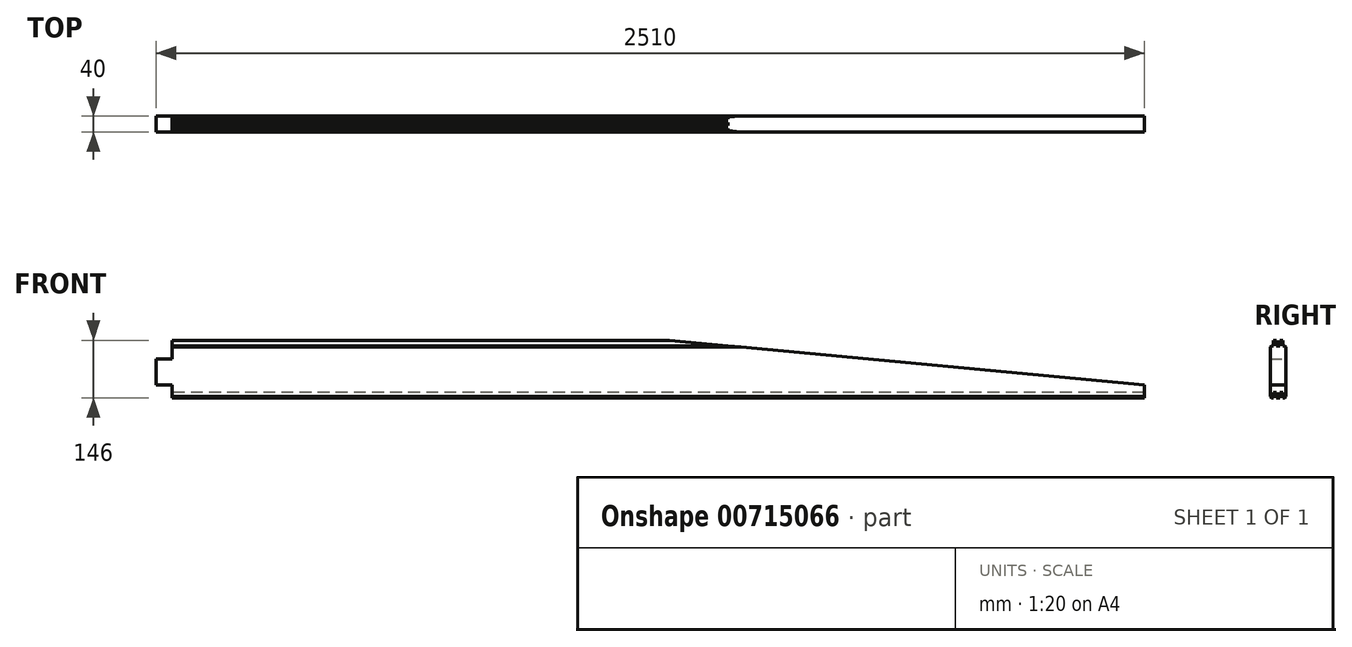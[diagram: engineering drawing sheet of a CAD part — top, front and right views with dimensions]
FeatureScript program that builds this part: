
annotation { "Feature Type Name" : "Feature", "Feature Type Description" : "" }
export const myFeature = defineFeature(function(context is Context, id is Id, definition is map)
    precondition{}
    {
        {
            assignVariable(context, id + "F0", {"name" : "Laenge", "anyValue" : 2550});
        }
        {
            var Q0;
            Q0=qCreatedBy(makeId("Right.planeOp"),FACE);
            var sketch = newSketch(context, id + "F1", { "sketchPlane" : qUnion([Q0])});
            skLineSegment(sketch, "E0", {"start": v(20, 63) * mm, "end": v(20, -63) * mm});
            skLineSegment(sketch, "E1", {"start": v(20, -63) * mm, "end": v(17, -66) * mm});
            skLineSegment(sketch, "E2", {"start": v(17, -66) * mm, "end": v(12, -66) * mm});
            skLineSegment(sketch, "E3", {"start": v(12, -52) * mm, "end": v(12, -66) * mm});
            skLineSegment(sketch, "E4", {"start": v(12, -52) * mm, "end": v(4, -52) * mm});
            skLineSegment(sketch, "E5", {"start": v(4, -66) * mm, "end": v(4, -52) * mm});
            skLineSegment(sketch, "E6", {"start": v(4, -66) * mm, "end": v(-4, -66) * mm});
            skLineSegment(sketch, "E7", {"start": v(-4, -52) * mm, "end": v(-4, -66) * mm});
            skLineSegment(sketch, "E8", {"start": v(-4, -52) * mm, "end": v(-12, -52) * mm});
            skLineSegment(sketch, "E9", {"start": v(-12, -66) * mm, "end": v(-12, -52) * mm});
            skLineSegment(sketch, "E10", {"start": v(-12, -66) * mm, "end": v(-17, -66) * mm});
            skLineSegment(sketch, "E11", {"start": v(-17, -66) * mm, "end": v(-20, -63) * mm});
            skLineSegment(sketch, "E12", {"start": v(-20, -63) * mm, "end": v(-20, 63) * mm});
            skLineSegment(sketch, "E13", {"start": v(-20, 63) * mm, "end": v(-17, 66) * mm});
            skLineSegment(sketch, "E14", {"start": v(-17, 66) * mm, "end": v(-12, 66) * mm});
            skLineSegment(sketch, "E15", {"start": v(-4, 66) * mm, "end": v(4, 66) * mm});
            skLineSegment(sketch, "E16", {"start": v(12, 66) * mm, "end": v(17, 66) * mm});
            skLineSegment(sketch, "E17", {"start": v(17, 66) * mm, "end": v(20, 63) * mm});
            skPoint(sketch, "E18.end.orphan", {"position": v(12, 57.8) * mm});
            skPoint(sketch, "E19.end.orphan", {"position": v(4, 66.3) * mm});
            skPoint(sketch, "E20.end.orphan", {"position": v(-4, 66.3) * mm});
            skLineSegment(sketch, "E21", {"start": v(-12, 66) * mm, "end": v(-12, 80) * mm});
            skLineSegment(sketch, "E22", {"start": v(-12, 80) * mm, "end": v(-4, 80) * mm});
            skLineSegment(sketch, "E23", {"start": v(-4, 80) * mm, "end": v(-4, 66) * mm});
            skLineSegment(sketch, "E24", {"start": v(4, 66) * mm, "end": v(4, 80) * mm});
            skLineSegment(sketch, "E25", {"start": v(4, 80) * mm, "end": v(12, 80) * mm});
            skLineSegment(sketch, "E26", {"start": v(12, 80) * mm, "end": v(12, 66) * mm});
            skLineSegment(sketch, "E27", {"start": v(20, -33) * mm, "end": v(-20, -33) * mm});
            skLineSegment(sketch, "E28", {"start": v(20, 33) * mm, "end": v(-20, 33) * mm});
            skPoint(sketch, "E29.end.orphan", {"position": v(-141.42, 0) * mm});
            skLineSegment(sketch, "E30", {"start": v(20, 0) * mm, "end": v(-20, 0) * mm});
            skLineSegment(sketch, "E31", {"start": v(20, 0) * mm, "end": v(-20, 0) * mm, "construction": true});
            skLineSegment(sketch, "E32", {"start": v(0, 33) * mm, "end": v(0, -33) * mm, "construction": true});
            skSolve(sketch);
        }
        {
            var Q0;
            Q0=qCreatedBy(makeId("Front.planeOp"),FACE);
            var sketch = newSketch(context, id + "F2", { "sketchPlane" : qUnion([Q0])});
            skLineSegment(sketch, "E33", {"start": v(1275, 0) * mm, "end": v(-1275, 0) * mm, "construction": true});
            skPoint(sketch, "E34.right.start.orphan", {"position": v(-259.12, 108.1) * mm});
            skPoint(sketch, "E35.left.start.orphan", {"position": v(237.35, 108.1) * mm});
            skPoint(sketch, "E36.left.end.orphan", {"position": v(237.35, -84.05) * mm});
            skPoint(sketch, "E36.bottom.start.orphan", {"position": v(237.35, -117.05) * mm});
            skPoint(sketch, "E37.right.start.orphan", {"position": v(-259.12, -117.05) * mm});
            skPoint(sketch, "E37.top.end.orphan", {"position": v(-259.12, -84.05) * mm});
            skLineSegment(sketch, "E38.bottom", {"start": v(-1315, 33) * mm, "end": v(-1235, 33) * mm});
            skLineSegment(sketch, "E38.top", {"start": v(-1315, 133) * mm, "end": v(-1235, 133) * mm});
            skLineSegment(sketch, "E38.left", {"start": v(-1315, 33) * mm, "end": v(-1315, 133) * mm});
            skLineSegment(sketch, "E38.right", {"start": v(-1235, 33) * mm, "end": v(-1235, 133) * mm});
            skPoint(sketch, "E38.middle", {"position": v(-1275, 83) * mm});
            skLineSegment(sketch, "E39.bottom", {"start": v(-1315, -133) * mm, "end": v(-1235, -133) * mm});
            skLineSegment(sketch, "E39.top", {"start": v(-1315, -33) * mm, "end": v(-1235, -33) * mm});
            skLineSegment(sketch, "E39.left", {"start": v(-1315, -133) * mm, "end": v(-1315, -33) * mm});
            skLineSegment(sketch, "E39.right", {"start": v(-1235, -133) * mm, "end": v(-1235, -33) * mm});
            skPoint(sketch, "E39.middle", {"position": v(-1275, -83) * mm});
            skLineSegment(sketch, "E40.bottom", {"start": v(1315, 33) * mm, "end": v(1235, 33) * mm});
            skLineSegment(sketch, "E40.top", {"start": v(1315, 133) * mm, "end": v(1235, 133) * mm});
            skLineSegment(sketch, "E40.left", {"start": v(1315, 33) * mm, "end": v(1315, 133) * mm});
            skLineSegment(sketch, "E40.right", {"start": v(1235, 33) * mm, "end": v(1235, 133) * mm});
            skPoint(sketch, "E40.middle", {"position": v(1275, 83) * mm});
            skLineSegment(sketch, "E41.bottom", {"start": v(1315, -33) * mm, "end": v(1235, -33) * mm});
            skLineSegment(sketch, "E41.top", {"start": v(1315, -133) * mm, "end": v(1235, -133) * mm});
            skLineSegment(sketch, "E41.left", {"start": v(1315, -33) * mm, "end": v(1315, -133) * mm});
            skLineSegment(sketch, "E41.right", {"start": v(1235, -33) * mm, "end": v(1235, -133) * mm});
            skPoint(sketch, "E41.middle", {"position": v(1275, -83) * mm});
            skSolve(sketch);
        }
        {
            var Q0;
            {var subQ3=sQuery(id+"F1.wireOp",EDGE,"E13");Q0=makeQuery(id+"F1.imprint","IMPRINT",FACE,{"disambiguationData":[TD([[makeQuery(id+"F1.imprint","IMPRINT",EDGE,{"derivedFrom":subQ3}),-1.0]])]});}
            var Q1;
            {var subQ0=sQuery(id+"F1.wireOp",EDGE,"E28");Q1=makeQuery(id+"F1.imprint","IMPRINT",FACE,{"disambiguationData":[TD([[makeQuery(id+"F1.imprint","IMPRINT",EDGE,{"derivedFrom":subQ0}),1.0]])]});}
            var Q2;
            {var subQ0=sQuery(id+"F1.wireOp",EDGE,"E27");Q2=makeQuery(id+"F1.imprint","IMPRINT",FACE,{"disambiguationData":[TD([[makeQuery(id+"F1.imprint","IMPRINT",EDGE,{"derivedFrom":subQ0}),-1.0]])]});}
            var Q3;
            {var subQ1=sQuery(id+"F1.wireOp",EDGE,"E1");Q3=makeQuery(id+"F1.imprint","IMPRINT",FACE,{"disambiguationData":[TD([[makeQuery(id+"F1.imprint","IMPRINT",EDGE,{"derivedFrom":subQ1}),-1.0]])]});}
            extrude(context, id + "F3", {"entities" : qUnion([Q0, Q1, Q2, Q3]), "endBound" : BoundingType.SYMMETRIC, "depth" : getVariable(context, 'Laenge') * mm, "offsetDistance" : 25 * mm});
        }
        {
            var Q0;
            Q0=makeQuery(id+"F2.imprint","IMPRINT",FACE,{"disambiguationData":[TD([[makeQuery(id+"F2.imprint","IMPRINT",EDGE,{"derivedFrom":sQuery(id+"F2.wireOp",EDGE,"E38.bottom")}),1.0]])]});
            var Q1;
            Q1=makeQuery(id+"F2.imprint","IMPRINT",FACE,{"disambiguationData":[TD([[makeQuery(id+"F2.imprint","IMPRINT",EDGE,{"derivedFrom":sQuery(id+"F2.wireOp",EDGE,"E39.bottom")}),1.0]])]});
            var Q2;
            Q2=makeQuery(id+"F2.imprint","IMPRINT",FACE,{"disambiguationData":[TD([[makeQuery(id+"F2.imprint","IMPRINT",EDGE,{"derivedFrom":sQuery(id+"F2.wireOp",EDGE,"E40.bottom")}),-1.0]])]});
            var Q3;
            Q3=makeQuery(id+"F2.imprint","IMPRINT",FACE,{"disambiguationData":[TD([[makeQuery(id+"F2.imprint","IMPRINT",EDGE,{"derivedFrom":sQuery(id+"F2.wireOp",EDGE,"E41.bottom")}),1.0]])]});
            extrude(context, id + "F4", {"entities" : qUnion([Q0, Q1, Q2, Q3]), "operationType" : NewBodyOperationType.REMOVE, "endBound" : BoundingType.SYMMETRIC, "oppositeDirection" : true, "depth" : 50 * mm, "offsetDistance" : 25 * mm});
        }
        {
            var Q0;
            Q0=qCreatedBy(makeId("Front.planeOp"),FACE);
            var sketch = newSketch(context, id + "F5", { "sketchPlane" : qUnion([Q0])});
            skLineSegment(sketch, "E42", {"start": v(-616.29, 140.37) * mm, "end": v(1375, -46.11) * mm});
            skLineSegment(sketch, "E43", {"start": v(-616.29, 140.37) * mm, "end": v(1375, 140.37) * mm});
            skLineSegment(sketch, "E44", {"start": v(1375, 140.37) * mm, "end": v(1375, -46.11) * mm});
            skSolve(sketch);
        }
        {
            var Q0;
            Q0=makeQuery(id+"F5.imprint","IMPRINT",FACE,{"disambiguationData":[TD([[makeQuery(id+"F5.imprint","IMPRINT",EDGE,{"derivedFrom":sQuery(id+"F5.wireOp",EDGE,"E42")}),1.0]])]});
            extrude(context, id + "F6", {"entities" : qUnion([Q0]), "operationType" : NewBodyOperationType.REMOVE, "endBound" : BoundingType.SYMMETRIC, "oppositeDirection" : true, "depth" : 50 * mm, "offsetDistance" : 25 * mm});
        }
    });
